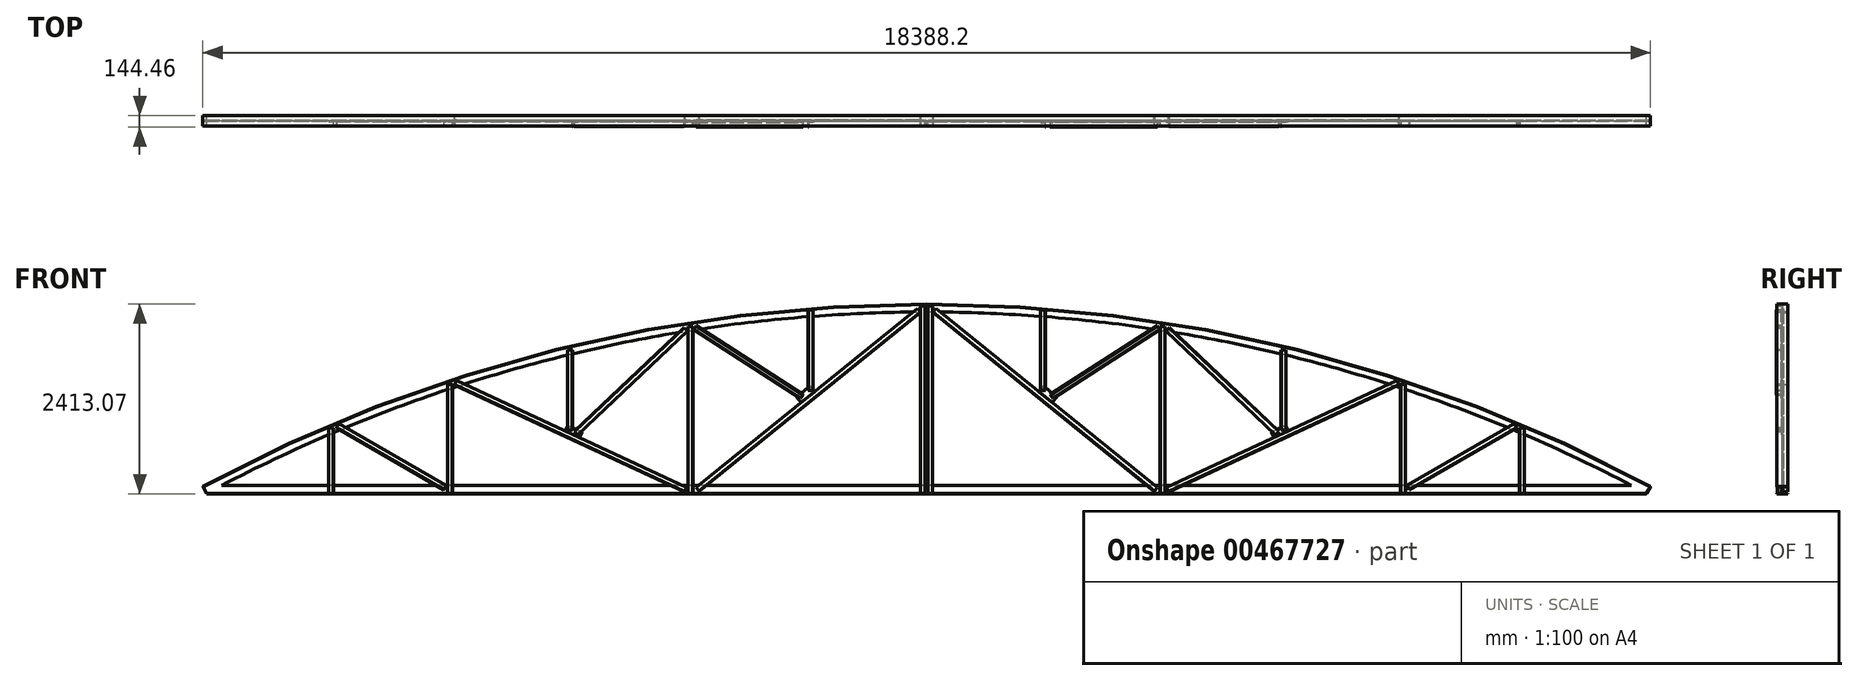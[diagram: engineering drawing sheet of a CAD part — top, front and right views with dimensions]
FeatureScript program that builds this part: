
annotation { "Feature Type Name" : "Feature", "Feature Type Description" : "" }
export const myFeature = defineFeature(function(context is Context, id is Id, definition is map)
    precondition{}
    {
        {
            var Q0;
            Q0=qCreatedBy(makeId("Front.planeOp"),FACE);
            var sketch = newSketch(context, id + "F0", { "sketchPlane" : qUnion([Q0])});
            skLineSegment(sketch, "E0", {"start": v(0, 0) * mm, "end": v(18288, 0) * mm});
            skArc(sketch, "E1", {"start": v(18288, 0) * mm, "mid": v(9144, 2305.05) * mm, "end": v(0, 0) * mm});
            skLineSegment(sketch, "E2", {"start": v(1612.9, 0) * mm, "end": v(1612.9, 774.13) * mm});
            skLineSegment(sketch, "E3", {"start": v(3092.45, 0) * mm, "end": v(3092.45, 1331.2) * mm});
            skLineSegment(sketch, "E4", {"start": v(6115.05, 0) * mm, "end": v(6115.05, 2065.75) * mm});
            skLineSegment(sketch, "E5", {"start": v(9144, 0) * mm, "end": v(9144, 2305.05) * mm});
            skLineSegment(sketch, "E6", {"start": v(7629.52, 1223.6) * mm, "end": v(7629.52, 2245.5) * mm});
            skLineSegment(sketch, "E7", {"start": v(3092.45, 0) * mm, "end": v(1692.88, 807.83) * mm});
            skLineSegment(sketch, "E8", {"start": v(6115.05, 0) * mm, "end": v(3187.59, 1362.37) * mm});
            skLineSegment(sketch, "E9", {"start": v(4651.32, 681.18) * mm, "end": v(4651.32, 1774.56) * mm});
            skLineSegment(sketch, "E10", {"start": v(4651.32, 681.18) * mm, "end": v(6115.05, 2065.75) * mm});
            skLineSegment(sketch, "E11", {"start": v(6190.76, 2077.64) * mm, "end": v(7580.54, 1184.02) * mm});
            skLineSegment(sketch, "E12.MirrorCS", {"start": v(12172.95, 0) * mm, "end": v(9144, 2305.05) * mm});
            skLineSegment(sketch, "E13.MirrorCS", {"start": v(10658.47, 1152.53) * mm, "end": v(10658.47, 2245.5) * mm});
            skLineSegment(sketch, "E14.MirrorCS", {"start": v(12097.24, 2077.64) * mm, "end": v(10658.47, 1152.52) * mm});
            skLineSegment(sketch, "E15.MirrorCS", {"start": v(12172.95, 0) * mm, "end": v(12172.95, 2065.75) * mm});
            skLineSegment(sketch, "E16.MirrorCS", {"start": v(13636.68, 681.18) * mm, "end": v(12172.95, 2065.75) * mm});
            skLineSegment(sketch, "E17.MirrorCS", {"start": v(13636.68, 681.18) * mm, "end": v(13636.68, 1774.56) * mm});
            skLineSegment(sketch, "E18.MirrorCS", {"start": v(12172.95, 0) * mm, "end": v(15100.41, 1362.37) * mm});
            skLineSegment(sketch, "E19.MirrorCS", {"start": v(15195.55, 0) * mm, "end": v(15195.55, 1331.2) * mm});
            skLineSegment(sketch, "E20.MirrorCS", {"start": v(15195.55, 0) * mm, "end": v(16595.12, 807.83) * mm});
            skLineSegment(sketch, "E21.MirrorCS", {"start": v(16675.1, 0) * mm, "end": v(16675.1, 774.13) * mm});
            skLineSegment(sketch, "E22", {"start": v(6115.05, 0) * mm, "end": v(8967.06, 2304.24) * mm});
            skPoint(sketch, "E23.end.orphan", {"position": v(7629.52, 1152.53) * mm});
            skSolve(sketch);
        }
        {
            var Q0;
            Q0=qCreatedBy(makeId("Right.planeOp"),FACE);
            var sketch = newSketch(context, id + "F1", { "sketchPlane" : qUnion([Q0])});
            skLineSegment(sketch, "E24.bottom", {"start": v(-68.26, -3.18) * mm, "end": v(68.26, -3.18) * mm});
            skLineSegment(sketch, "E24.top", {"start": v(-68.26, 3.18) * mm, "end": v(-3.17, 3.18) * mm});
            skLineSegment(sketch, "E24.left", {"start": v(-68.26, -3.18) * mm, "end": v(-68.26, 3.18) * mm});
            skLineSegment(sketch, "E24.right", {"start": v(68.26, -3.18) * mm, "end": v(68.26, 3.18) * mm});
            skPoint(sketch, "E24.middle", {"position": v(0, 0) * mm});
            skLineSegment(sketch, "E25.top", {"start": v(-3.18, 104.78) * mm, "end": v(3.17, 104.78) * mm});
            skLineSegment(sketch, "E25.left", {"start": v(-3.17, 3.18) * mm, "end": v(-3.18, 104.78) * mm});
            skLineSegment(sketch, "E25.right", {"start": v(3.18, 3.18) * mm, "end": v(3.17, 104.78) * mm});
            skLineSegment(sketch, "E26.trimOffspring", {"start": v(3.17, 3.18) * mm, "end": v(68.26, 3.18) * mm});
            skSolve(sketch);
        }
        {
            var Q0;
            Q0=qSketchRegion(id+"F1",true);
            var Q1;
            Q1=sQuery(id+"F0.wireOp",VERTEX,"E1.start");
            extrude(context, id + "F2", {"entities" : qUnion([Q0]), "endBound" : BoundingType.UP_TO_VERTEX, "endBoundEntityVertex" : qUnion([Q1]), "depth" : 25.4 * mm});
        }
        {
            var Q0;
            Q0=sQuery(id+"F0.wireOp",EDGE,"E1");
            var Q1;
            Q1=sQuery(id+"F0.wireOp",VERTEX,"E0.start");
            cPlane(context, id + "F3", {"entities" : qUnion([Q0, Q1]), "cplaneType" : CPlaneType.CURVE_POINT, "offset" : 25.4 * mm, "width" : 152.4 * mm, "height" : 152.4 * mm});
        }
        {
            var Q0;
            Q0=qCreatedBy(id+"F3.planeOp",FACE);
            var sketch = newSketch(context, id + "F4", { "sketchPlane" : qUnion([Q0])});
            skPoint(sketch, "E27.middle", {"position": v(0, 0) * mm});
            skLineSegment(sketch, "E28.left", {"start": v(3.18, 3.25) * mm, "end": v(3.17, 98.5) * mm});
            skLineSegment(sketch, "E28.right", {"start": v(-3.17, 3.25) * mm, "end": v(-3.18, 98.5) * mm});
            skLineSegment(sketch, "E29", {"start": v(-3.17, 3.25) * mm, "end": v(3.18, 3.25) * mm});
            skLineSegment(sketch, "E30", {"start": v(68.26, 104.85) * mm, "end": v(68.26, 98.5) * mm});
            skLineSegment(sketch, "E31", {"start": v(68.26, 98.5) * mm, "end": v(3.17, 98.5) * mm});
            skLineSegment(sketch, "E32", {"start": v(-68.26, 104.85) * mm, "end": v(-68.26, 98.5) * mm});
            skLineSegment(sketch, "E33", {"start": v(-68.26, 98.5) * mm, "end": v(-3.18, 98.5) * mm});
            skPoint(sketch, "E34.0", {"position": v(68.26, -2.8) * mm});
            skPoint(sketch, "E34.1", {"position": v(-68.26, -2.8) * mm});
            skLineSegment(sketch, "E35", {"start": v(-68.26, 104.85) * mm, "end": v(68.26, 104.85) * mm});
            skSolve(sketch);
        }
        {
            var Q0;
            Q0=makeQuery(id+"F4.imprint","IMPRINT",FACE,{"disambiguationData":[TD([[makeQuery(id+"F4.imprint","IMPRINT",EDGE,{"derivedFrom":sQuery(id+"F4.wireOp",EDGE,"E28.left")}),1.0]])]});
            var Q1;
            Q1=sQuery(id+"F0.wireOp",EDGE,"E1");
            sweep(context, id + "F5", {"profiles" : qUnion([Q0]), "path" : qUnion([Q1])});
        }
        {
            var Q0;
            Q0=sQuery(id+"F0.wireOp",EDGE,"E2");
            var Q1;
            Q1=sQuery(id+"F0.wireOp",VERTEX,"E2.start");
            cPlane(context, id + "F6", {"entities" : qUnion([Q0, Q1]), "cplaneType" : CPlaneType.CURVE_POINT, "offset" : 25.4 * mm, "width" : 152.4 * mm, "height" : 152.4 * mm});
        }
        {
            var Q0;
            Q0=qCreatedBy(id+"F6.planeOp",FACE);
            var sketch = newSketch(context, id + "F7", { "sketchPlane" : qUnion([Q0])});
            skLineSegment(sketch, "E36", {"start": v(1612.9, -66.68) * mm, "end": v(1606.55, -66.68) * mm});
            skLineSegment(sketch, "E37", {"start": v(1606.55, -66.68) * mm, "end": v(1606.55, -9.53) * mm});
            skPoint(sketch, "E38.bottom.start.orphan", {"position": v(1606.55, 0) * mm});
            skLineSegment(sketch, "E39", {"start": v(1612.9, -3.17) * mm, "end": v(1612.9, -66.68) * mm});
            skPoint(sketch, "E40.0", {"position": v(1612.9, 0) * mm});
            skLineSegment(sketch, "E41", {"start": v(1606.55, -9.53) * mm, "end": v(1549.4, -9.53) * mm});
            skLineSegment(sketch, "E42", {"start": v(1549.4, 0) * mm, "end": v(1612.9, 0) * mm});
            skLineSegment(sketch, "E43", {"start": v(1549.4, -3.18) * mm, "end": v(1612.9, -3.17) * mm});
            skPoint(sketch, "E44.start.orphan", {"position": v(1549.4, -6.35) * mm});
            skLineSegment(sketch, "E45", {"start": v(1549.4, -9.53) * mm, "end": v(1549.4, -3.18) * mm});
            skSolve(sketch);
        }
        {
            var Q0;
            Q0=qSketchRegion(id+"F7",true);
            extrude(context, id + "F8", {"entities" : qUnion([Q0]), "operationType" : NewBodyOperationType.ADD, "depth" : 838.2 * mm});
        }
        {
            var Q0;
            Q0=sQuery(id+"F0.wireOp",EDGE,"E7");
            var Q1;
            Q1=sQuery(id+"F0.wireOp",VERTEX,"E3.start");
            cPlane(context, id + "F9", {"entities" : qUnion([Q0, Q1]), "cplaneType" : CPlaneType.CURVE_POINT, "offset" : 25.4 * mm, "width" : 152.4 * mm, "height" : 152.4 * mm});
        }
        {
            var Q0;
            Q0=qCreatedBy(id+"F9.planeOp",FACE);
            var sketch = newSketch(context, id + "F10", { "sketchPlane" : qUnion([Q0])});
            skPoint(sketch, "E46.0", {"position": v(2.83, 1546.43) * mm});
            skLineSegment(sketch, "E47", {"start": v(3.18, 1545.92) * mm, "end": v(66.67, 1545.92) * mm});
            skLineSegment(sketch, "E48", {"start": v(66.67, 1545.92) * mm, "end": v(66.67, 1552.27) * mm});
            skLineSegment(sketch, "E49", {"start": v(66.67, 1552.27) * mm, "end": v(9.52, 1552.27) * mm});
            skLineSegment(sketch, "E50", {"start": v(9.52, 1552.27) * mm, "end": v(9.52, 1609.42) * mm});
            skLineSegment(sketch, "E51", {"start": v(9.52, 1609.42) * mm, "end": v(3.17, 1609.42) * mm});
            skLineSegment(sketch, "E52", {"start": v(3.17, 1609.42) * mm, "end": v(3.17, 1545.92) * mm});
            skSolve(sketch);
        }
        {
            var Q0;
            Q0=qSketchRegion(id+"F10",true);
            extrude(context, id + "F11", {"entities" : qUnion([Q0]), "depth" : 1574.8 * mm});
        }
        {
            var Q0;
            Q0=sQuery(id+"F0.wireOp",EDGE,"E3");
            var Q1;
            Q1=sQuery(id+"F0.wireOp",VERTEX,"E7.start");
            cPlane(context, id + "F12", {"entities" : qUnion([Q0, Q1]), "cplaneType" : CPlaneType.CURVE_POINT, "offset" : 25.4 * mm, "width" : 152.4 * mm, "height" : 152.4 * mm});
        }
        {
            var Q0;
            Q0=qCreatedBy(id+"F12.planeOp",FACE);
            var sketch = newSketch(context, id + "F13", { "sketchPlane" : qUnion([Q0])});
            skLineSegment(sketch, "E53", {"start": v(3124.65, -66.68) * mm, "end": v(3124.65, -9.53) * mm});
            skLineSegment(sketch, "E54", {"start": v(3124.65, -66.67) * mm, "end": v(3118.3, -66.67) * mm});
            skLineSegment(sketch, "E55", {"start": v(3118.3, -9.53) * mm, "end": v(3118.3, -66.67) * mm});
            skLineSegment(sketch, "E56", {"start": v(3118.3, -3.17) * mm, "end": v(3061.15, -3.18) * mm});
            skLineSegment(sketch, "E57", {"start": v(3061.15, -3.18) * mm, "end": v(3061.15, -9.53) * mm});
            skLineSegment(sketch, "E58", {"start": v(3061.15, -9.53) * mm, "end": v(3118.3, -9.53) * mm});
            skLineSegment(sketch, "E59", {"start": v(3124.65, -9.53) * mm, "end": v(3124.65, -3.17) * mm});
            skLineSegment(sketch, "E60", {"start": v(3124.65, -3.17) * mm, "end": v(3118.3, -3.17) * mm});
            skSolve(sketch);
        }
        {
            var Q0;
            Q0=qSketchRegion(id+"F13",true);
            extrude(context, id + "F14", {"entities" : qUnion([Q0]), "depth" : 1386.84 * mm});
        }
        {
            var Q0;
            Q0=makeQuery(id+"F11.opExtrude","SWEPT_BODY",BODY,{"disambiguationData":[OSD([sQuery(id+"F10.wireOp",EDGE,"E47"),sQuery(id+"F10.wireOp",EDGE,"E48"),sQuery(id+"F10.wireOp",EDGE,"E49"),sQuery(id+"F10.wireOp",EDGE,"E50"),sQuery(id+"F10.wireOp",EDGE,"E51"),sQuery(id+"F10.wireOp",EDGE,"E52")])]});
            var Q1;
            Q1=sQuery(id+"F0.wireOp",EDGE,"E7");
            var Q2;
            Q2=sQuery(id+"F0.wireOp",EDGE,"E7");
            transform(context, id + "F15", {"entities" : qUnion([Q0]), "transformType" : TransformType.TRANSLATION_DISTANCE, "transformDirection" : qUnion([Q2]), "distance" : 95.25 * mm, "makeCopy" : false});
        }
        {
            var Q0;
            Q0=sQuery(id+"F0.wireOp",EDGE,"E8");
            var Q1;
            Q1=sQuery(id+"F0.wireOp",VERTEX,"E8.start");
            cPlane(context, id + "F16", {"entities" : qUnion([Q0, Q1]), "cplaneType" : CPlaneType.CURVE_POINT, "offset" : 25.4 * mm, "width" : 152.4 * mm, "height" : 152.4 * mm});
        }
        {
            var Q0;
            Q0=qCreatedBy(id+"F16.planeOp",FACE);
            cPlane(context, id + "F17", {"entities" : qUnion([Q0]), "cplaneType" : CPlaneType.OFFSET, "offset" : 50.8 * mm, "width" : 152.4 * mm, "height" : 152.4 * mm});
        }
        {
            var Q0;
            Q0=qCreatedBy(id+"F17.planeOp",FACE);
            var sketch = newSketch(context, id + "F18", { "sketchPlane" : qUnion([Q0])});
            skPoint(sketch, "E61.0", {"position": v(0, 2580.09) * mm});
            skLineSegment(sketch, "E62.MirrorCS", {"start": v(-3.18, 2580.09) * mm, "end": v(-3.18, 2643.59) * mm});
            skLineSegment(sketch, "E63.MirrorCS", {"start": v(-3.18, 2643.59) * mm, "end": v(-9.53, 2643.59) * mm});
            skLineSegment(sketch, "E64.MirrorCS", {"start": v(-9.53, 2643.59) * mm, "end": v(-9.53, 2586.44) * mm});
            skLineSegment(sketch, "E65.MirrorCS", {"start": v(-9.53, 2586.44) * mm, "end": v(-66.67, 2586.44) * mm});
            skLineSegment(sketch, "E66.MirrorCS", {"start": v(-66.67, 2586.44) * mm, "end": v(-66.67, 2580.09) * mm});
            skLineSegment(sketch, "E67.MirrorCS", {"start": v(-66.67, 2580.09) * mm, "end": v(-3.18, 2580.09) * mm});
            skLineSegment(sketch, "E68.MirrorCS", {"start": v(3.18, 2643.59) * mm, "end": v(9.53, 2643.59) * mm});
            skLineSegment(sketch, "E69.MirrorCS", {"start": v(66.67, 2586.44) * mm, "end": v(66.67, 2580.09) * mm});
            skLineSegment(sketch, "E70.MirrorCS", {"start": v(66.67, 2580.09) * mm, "end": v(3.18, 2580.09) * mm});
            skLineSegment(sketch, "E71.MirrorCS", {"start": v(3.18, 2580.09) * mm, "end": v(3.18, 2643.59) * mm});
            skLineSegment(sketch, "E72.MirrorCS", {"start": v(9.53, 2586.44) * mm, "end": v(66.67, 2586.44) * mm});
            skLineSegment(sketch, "E73.MirrorCS", {"start": v(9.53, 2643.59) * mm, "end": v(9.53, 2586.44) * mm});
            skSolve(sketch);
        }
        {
            var Q0;
            Q0=qSketchRegion(id+"F18",true);
            extrude(context, id + "F19", {"entities" : qUnion([Q0]), "depth" : 3225.8 * mm});
        }
        {
            var Q0;
            Q0=sQuery(id+"F0.wireOp",EDGE,"E8");
            cPoint(context, id + "F20", {"entities" : qUnion([Q0]), "parameter" : 0.5});
        }
        {
            var Q0;
            Q0=sQuery(id+"F0.wireOp",EDGE,"E9");
            var Q1;
            Q1=qCreatedBy(id+"F20",VERTEX);
            cPlane(context, id + "F21", {"entities" : qUnion([Q0, Q1]), "cplaneType" : CPlaneType.CURVE_POINT, "offset" : 25.4 * mm, "width" : 152.4 * mm, "height" : 152.4 * mm});
        }
        {
            var Q0;
            Q0=qCreatedBy(id+"F21.planeOp",FACE);
            cPlane(context, id + "F22", {"entities" : qUnion([Q0]), "cplaneType" : CPlaneType.OFFSET, "offset" : 127 * mm, "width" : 152.4 * mm, "height" : 152.4 * mm});
        }
        {
            var Q0;
            Q0=qCreatedBy(id+"F22.planeOp",FACE);
            var sketch = newSketch(context, id + "F23", { "sketchPlane" : qUnion([Q0])});
            skLineSegment(sketch, "E74", {"start": v(4644.56, -9.53) * mm, "end": v(4644.56, -73.03) * mm});
            skLineSegment(sketch, "E75", {"start": v(4644.56, -73.03) * mm, "end": v(4638.21, -73.03) * mm});
            skLineSegment(sketch, "E76", {"start": v(4638.21, -73.03) * mm, "end": v(4638.21, -15.88) * mm});
            skLineSegment(sketch, "E77", {"start": v(4638.21, -15.88) * mm, "end": v(4581.06, -15.88) * mm});
            skLineSegment(sketch, "E78", {"start": v(4581.06, -15.88) * mm, "end": v(4581.06, -9.53) * mm});
            skLineSegment(sketch, "E79", {"start": v(4581.06, -9.53) * mm, "end": v(4644.56, -9.53) * mm});
            skLineSegment(sketch, "E80.0", {"start": v(3144.76, -9.53) * mm, "end": v(6117.73, -9.53) * mm});
            skSolve(sketch);
        }
        {
            var Q0;
            Q0=qSketchRegion(id+"F23",true);
            extrude(context, id + "F24", {"entities" : qUnion([Q0]), "operationType" : NewBodyOperationType.ADD, "depth" : 1016 * mm});
        }
        {
            var Q0;
            Q0=sQuery(id+"F0.wireOp",EDGE,"E10");
            var Q1;
            Q1=sQuery(id+"F0.wireOp",VERTEX,"E10.start");
            cPlane(context, id + "F25", {"entities" : qUnion([Q0, Q1]), "cplaneType" : CPlaneType.CURVE_POINT, "offset" : 25.4 * mm, "width" : 152.4 * mm, "height" : 152.4 * mm});
        }
        {
            var Q0;
            Q0=qCreatedBy(id+"F25.planeOp",FACE);
            cPlane(context, id + "F26", {"entities" : qUnion([Q0]), "cplaneType" : CPlaneType.OFFSET, "offset" : 88.9 * mm, "width" : 152.4 * mm, "height" : 152.4 * mm});
        }
        {
            var Q0;
            Q0=qCreatedBy(id+"F26.planeOp",FACE);
            var sketch = newSketch(context, id + "F27", { "sketchPlane" : qUnion([Q0])});
            skLineSegment(sketch, "E81.0", {"start": v(0.48, -1133.42) * mm, "end": v(0.48, -4181.53) * mm});
            skLineSegment(sketch, "E82", {"start": v(-9.05, -2695.12) * mm, "end": v(-9.05, -2631.62) * mm});
            skLineSegment(sketch, "E83", {"start": v(-9.05, -2631.62) * mm, "end": v(-72.55, -2631.62) * mm});
            skLineSegment(sketch, "E84", {"start": v(-72.55, -2631.62) * mm, "end": v(-72.55, -2637.97) * mm});
            skLineSegment(sketch, "E85", {"start": v(-72.55, -2637.97) * mm, "end": v(-15.4, -2637.97) * mm});
            skLineSegment(sketch, "E86", {"start": v(-15.4, -2637.97) * mm, "end": v(-15.4, -2695.12) * mm});
            skLineSegment(sketch, "E87", {"start": v(-15.4, -2695.12) * mm, "end": v(-9.05, -2695.12) * mm});
            skPoint(sketch, "E88.end.orphan", {"position": v(13.18, -2683.97) * mm});
            skSolve(sketch);
        }
        {
            var Q0;
            Q0=qSketchRegion(id+"F27",true);
            extrude(context, id + "F28", {"entities" : qUnion([Q0]), "depth" : 1917.7 * mm});
        }
        {
            var Q0;
            Q0=makeQuery(id+"F19.opExtrude","SWEPT_FACE",FACE,{"disambiguationData":[OSD([sQuery(id+"F18.wireOp",EDGE,"E68.MirrorCS")])]});
            var sketch = newSketch(context, id + "F29", { "sketchPlane" : qUnion([Q0])});
            skLineSegment(sketch, "E89.bottom", {"start": v(3789.84, -9.53) * mm, "end": v(3993.04, -9.53) * mm});
            skLineSegment(sketch, "E89.top", {"start": v(3789.84, -3.17) * mm, "end": v(3993.04, -3.17) * mm});
            skLineSegment(sketch, "E89.left", {"start": v(3789.84, -9.53) * mm, "end": v(3789.84, -3.17) * mm});
            skLineSegment(sketch, "E89.right", {"start": v(3993.04, -9.53) * mm, "end": v(3993.04, -3.17) * mm});
            skSolve(sketch);
        }
        {
            var Q0;
            Q0=qSketchRegion(id+"F29",true);
            extrude(context, id + "F30", {"entities" : qUnion([Q0]), "depth" : 76.96 * mm});
        }
        {
            var Q0;
            Q0=makeQuery(id+"F2.opExtrude","SWEPT_FACE",FACE,{"disambiguationData":[OSD([sQuery(id+"F1.wireOp",EDGE,"E24.top")])]});
            cPlane(context, id + "F31", {"entities" : qUnion([Q0]), "cplaneType" : CPlaneType.OFFSET, "offset" : 0 * mm, "width" : 152.4 * mm, "height" : 152.4 * mm});
        }
        {
            var Q0;
            Q0=qCreatedBy(id+"F31.planeOp",FACE);
            var sketch = newSketch(context, id + "F32", { "sketchPlane" : qUnion([Q0])});
            skPoint(sketch, "E90.0", {"position": v(6115.05, 0) * mm});
            skLineSegment(sketch, "E91", {"start": v(6115.05, -3.18) * mm, "end": v(6178.55, -3.18) * mm});
            skLineSegment(sketch, "E92", {"start": v(6178.55, -3.18) * mm, "end": v(6178.55, -9.53) * mm});
            skLineSegment(sketch, "E93", {"start": v(6115.05, -9.53) * mm, "end": v(6115.05, -3.17) * mm});
            skLineSegment(sketch, "E94", {"start": v(6178.55, -9.53) * mm, "end": v(6178.55, -66.67) * mm});
            skLineSegment(sketch, "E95", {"start": v(6178.55, -66.67) * mm, "end": v(6172.2, -66.67) * mm});
            skLineSegment(sketch, "E96", {"start": v(6172.2, -66.67) * mm, "end": v(6172.2, -9.53) * mm});
            skPoint(sketch, "E97.start.orphan", {"position": v(6122.79, -66.68) * mm});
            skPoint(sketch, "E98.orphan", {"position": v(6115.05, -66.67) * mm});
            skLineSegment(sketch, "E99", {"start": v(6115.05, -9.53) * mm, "end": v(6172.2, -9.53) * mm});
            skSolve(sketch);
        }
        {
            var Q0;
            Q0=qSketchRegion(id+"F32",true);
            extrude(context, id + "F33", {"entities" : qUnion([Q0]), "depth" : 2120.9 * mm});
        }
        {
            var Q0;
            Q0=makeQuery(id+"F2.opExtrude","SWEPT_FACE",FACE,{"disambiguationData":[OSD([sQuery(id+"F1.wireOp",EDGE,"E24.top")])]});
            var sketch = newSketch(context, id + "F34", { "sketchPlane" : qUnion([Q0])});
            skPoint(sketch, "E100.0", {"position": v(9144, 0) * mm});
            skLineSegment(sketch, "E101.0", {"start": v(0, 0) * mm, "end": v(18288, 0) * mm});
            skLineSegment(sketch, "E102", {"start": v(9131.7, -3.17) * mm, "end": v(9131.7, -66.67) * mm});
            skLineSegment(sketch, "E103", {"start": v(9131.7, -66.67) * mm, "end": v(9125.35, -66.67) * mm});
            skLineSegment(sketch, "E104", {"start": v(9125.35, -66.67) * mm, "end": v(9125.35, -9.52) * mm});
            skLineSegment(sketch, "E105", {"start": v(9125.35, -9.52) * mm, "end": v(9068.2, -9.53) * mm});
            skLineSegment(sketch, "E106", {"start": v(9068.2, -9.53) * mm, "end": v(9068.2, -3.18) * mm});
            skLineSegment(sketch, "E107", {"start": v(9068.2, -3.17) * mm, "end": v(9131.7, -3.17) * mm});
            skSolve(sketch);
        }
        {
            var Q0;
            Q0=makeQuery(id+"F34.imprint","IMPRINT",FACE,{"disambiguationData":[TD([[makeQuery(id+"F34.imprint","IMPRINT",EDGE,{"derivedFrom":sQuery(id+"F34.wireOp",EDGE,"E102")}),-1.0]])]});
            extrude(context, id + "F35", {"entities" : qUnion([Q0]), "operationType" : NewBodyOperationType.ADD, "depth" : 2379.98 * mm});
        }
        {
            var Q0;
            Q0=sQuery(id+"F0.wireOp",EDGE,"E22");
            var Q1;
            Q1=sQuery(id+"F0.wireOp",VERTEX,"E4.start");
            cPlane(context, id + "F36", {"entities" : qUnion([Q0, Q1]), "cplaneType" : CPlaneType.CURVE_POINT, "offset" : 25.4 * mm, "width" : 152.4 * mm, "height" : 152.4 * mm});
        }
        {
            var Q0;
            Q0=qCreatedBy(id+"F36.planeOp",FACE);
            cPlane(context, id + "F37", {"entities" : qUnion([Q0]), "cplaneType" : CPlaneType.OFFSET, "offset" : 129.54 * mm, "width" : 152.4 * mm, "height" : 152.4 * mm});
        }
        {
            var Q0;
            Q0=qCreatedBy(id+"F37.planeOp",FACE);
            var sketch = newSketch(context, id + "F38", { "sketchPlane" : qUnion([Q0])});
            skPoint(sketch, "E108.0", {"position": v(0, -3843) * mm});
            skLineSegment(sketch, "E109", {"start": v(0, -3843) * mm, "end": v(-4.09, -3843) * mm});
            skLineSegment(sketch, "E110", {"start": v(-4.09, -3843) * mm, "end": v(-4.09, -3906.5) * mm});
            skLineSegment(sketch, "E111", {"start": v(-4.09, -3906.5) * mm, "end": v(-67.59, -3906.5) * mm});
            skLineSegment(sketch, "E112", {"start": v(-67.59, -3906.5) * mm, "end": v(-67.59, -3900.16) * mm});
            skLineSegment(sketch, "E113", {"start": v(-67.59, -3900.16) * mm, "end": v(-10.44, -3900.16) * mm});
            skLineSegment(sketch, "E114", {"start": v(-10.44, -3900.16) * mm, "end": v(-10.44, -3843) * mm});
            skLineSegment(sketch, "E115", {"start": v(-10.44, -3843) * mm, "end": v(-4.09, -3843) * mm});
            skLineSegment(sketch, "E116.MirrorCS", {"start": v(4.09, -3843) * mm, "end": v(4.09, -3906.5) * mm});
            skLineSegment(sketch, "E117.MirrorCS", {"start": v(10.44, -3900.16) * mm, "end": v(10.44, -3843) * mm});
            skLineSegment(sketch, "E118.MirrorCS", {"start": v(67.59, -3900.16) * mm, "end": v(10.44, -3900.16) * mm});
            skLineSegment(sketch, "E119.MirrorCS", {"start": v(10.44, -3843) * mm, "end": v(4.09, -3843) * mm});
            skLineSegment(sketch, "E120.MirrorCS", {"start": v(4.09, -3906.5) * mm, "end": v(67.59, -3906.5) * mm});
            skLineSegment(sketch, "E121.MirrorCS", {"start": v(67.59, -3906.5) * mm, "end": v(67.59, -3900.16) * mm});
            skSolve(sketch);
        }
        {
            var Q0;
            Q0=qSketchRegion(id+"F38",true);
            extrude(context, id + "F39", {"entities" : qUnion([Q0]), "depth" : 3614.42 * mm});
        }
        {
            var Q0;
            Q0=sQuery(id+"F0.wireOp",EDGE,"E6");
            var Q1;
            Q1=sQuery(id+"F0.wireOp",VERTEX,"E23.end.orphan");
            cPlane(context, id + "F40", {"entities" : qUnion([Q0, Q1]), "cplaneType" : CPlaneType.CURVE_POINT, "offset" : 25.4 * mm, "width" : 152.4 * mm, "height" : 152.4 * mm});
        }
        {
            var Q0;
            Q0=qCreatedBy(id+"F40.planeOp",FACE);
            cPlane(context, id + "F41", {"entities" : qUnion([Q0]), "cplaneType" : CPlaneType.OFFSET, "offset" : 157.48 * mm, "width" : 152.4 * mm, "height" : 152.4 * mm});
        }
        {
            var Q0;
            Q0=qCreatedBy(id+"F41.planeOp",FACE);
            var sketch = newSketch(context, id + "F42", { "sketchPlane" : qUnion([Q0])});
            skLineSegment(sketch, "E122", {"start": v(7638.44, -76.2) * mm, "end": v(7638.44, -12.7) * mm});
            skLineSegment(sketch, "E123", {"start": v(7638.44, -76.2) * mm, "end": v(7644.79, -76.2) * mm});
            skLineSegment(sketch, "E124", {"start": v(7644.79, -19.05) * mm, "end": v(7644.79, -76.2) * mm});
            skLineSegment(sketch, "E125", {"start": v(7701.94, 0) * mm, "end": v(7638.44, 0) * mm});
            skLineSegment(sketch, "E126", {"start": v(7638.44, 0) * mm, "end": v(7701.94, 0) * mm});
            skPoint(sketch, "E127.0", {"position": v(7629.52, 0) * mm});
            skLineSegment(sketch, "E128", {"start": v(7701.94, -19.05) * mm, "end": v(7644.79, -19.05) * mm});
            skLineSegment(sketch, "E129", {"start": v(7701.94, -12.7) * mm, "end": v(7701.94, -19.05) * mm});
            skLineSegment(sketch, "E130", {"start": v(7638.44, -12.7) * mm, "end": v(7701.94, -12.7) * mm});
            skSolve(sketch);
        }
        {
            var Q0;
            Q0=qSketchRegion(id+"F42",true);
            extrude(context, id + "F43", {"entities" : qUnion([Q0]), "operationType" : NewBodyOperationType.ADD, "depth" : 1021.08 * mm});
        }
        {
            var Q0;
            Q0=sQuery(id+"F0.wireOp",EDGE,"E11");
            var Q1;
            Q1=sQuery(id+"F0.wireOp",VERTEX,"E23.end.orphan");
            cPlane(context, id + "F44", {"entities" : qUnion([Q0, Q1]), "cplaneType" : CPlaneType.CURVE_POINT, "offset" : 25.4 * mm, "width" : 152.4 * mm, "height" : 152.4 * mm});
        }
        {
            var Q0;
            Q0=qCreatedBy(id+"F44.planeOp",FACE);
            cPlane(context, id + "F45", {"entities" : qUnion([Q0]), "cplaneType" : CPlaneType.OFFSET, "offset" : 104.14 * mm, "oppositeDirection" : true, "width" : 152.4 * mm, "height" : 152.4 * mm});
        }
        {
            var Q0;
            Q0=qCreatedBy(id+"F45.planeOp",FACE);
            var sketch = newSketch(context, id + "F46", { "sketchPlane" : qUnion([Q0])});
            skLineSegment(sketch, "E131.0.1", {"start": v(0, 5095.74) * mm, "end": v(0, 5155.52) * mm});
            skLineSegment(sketch, "E131.0.2", {"start": v(0, 5155.52) * mm, "end": v(0, 6015.07) * mm});
            skLineSegment(sketch, "E131.0.3", {"start": v(0, 6015.07) * mm, "end": v(0, 5095.74) * mm});
            skLineSegment(sketch, "E132", {"start": v(-12.7, 5159.52) * mm, "end": v(-76.2, 5159.52) * mm});
            skLineSegment(sketch, "E133", {"start": v(-76.2, 5159.52) * mm, "end": v(-76.2, 5153.17) * mm});
            skLineSegment(sketch, "E134", {"start": v(-76.2, 5153.17) * mm, "end": v(-19.05, 5153.17) * mm});
            skLineSegment(sketch, "E135", {"start": v(-19.05, 5153.17) * mm, "end": v(-19.05, 5096.15) * mm});
            skLineSegment(sketch, "E136", {"start": v(-19.05, 5096.15) * mm, "end": v(-12.7, 5096.02) * mm});
            skLineSegment(sketch, "E137", {"start": v(0, 5159.52) * mm, "end": v(0, 5095.74) * mm});
            skLineSegment(sketch, "E138", {"start": v(-12.7, 5096.02) * mm, "end": v(-12.7, 5159.52) * mm});
            skSolve(sketch);
        }
        {
            var Q0;
            Q0=qSketchRegion(id+"F46",true);
            extrude(context, id + "F47", {"entities" : qUnion([Q0]), "operationType" : NewBodyOperationType.ADD, "oppositeDirection" : true, "depth" : 1617.98 * mm});
        }
        {
            var Q0;
            Q0=makeQuery(id+"F39.opExtrude","SWEPT_FACE",FACE,{"disambiguationData":[OSD([sQuery(id+"F38.wireOp",EDGE,"E115")])]});
            var sketch = newSketch(context, id + "F48", { "sketchPlane" : qUnion([Q0])});
            skLineSegment(sketch, "E139.bottom", {"start": v(6601.21, -10.44) * mm, "end": v(6817.11, -10.44) * mm});
            skLineSegment(sketch, "E139.top", {"start": v(6601.21, -4.09) * mm, "end": v(6817.11, -4.09) * mm});
            skLineSegment(sketch, "E139.left", {"start": v(6601.21, -10.44) * mm, "end": v(6601.21, -4.09) * mm});
            skLineSegment(sketch, "E139.right", {"start": v(6817.11, -10.44) * mm, "end": v(6817.11, -4.09) * mm});
            skSolve(sketch);
        }
        {
            var Q0;
            Q0=qSketchRegion(id+"F48",true);
            extrude(context, id + "F49", {"entities" : qUnion([Q0]), "depth" : 91.44 * mm});
        }
        {
            var Q0;
            Q0=makeQuery(id+"F35.opExtrude","SWEPT_FACE",FACE,{"disambiguationData":[OSD([sQuery(id+"F34.wireOp",EDGE,"E102")])]});
            cPlane(context, id + "F50", {"entities" : qUnion([Q0]), "cplaneType" : CPlaneType.OFFSET, "offset" : 12.7 * mm, "width" : 152.4 * mm, "height" : 152.4 * mm});
        }
        {
            var Q0;
            Q0=makeQuery(id+"F39.opExtrude","SWEPT_BODY",BODY,{"disambiguationData":[OSD([sQuery(id+"F38.wireOp",EDGE,"E110"),sQuery(id+"F38.wireOp",EDGE,"E111"),sQuery(id+"F38.wireOp",EDGE,"E112"),sQuery(id+"F38.wireOp",EDGE,"E113"),sQuery(id+"F38.wireOp",EDGE,"E114"),sQuery(id+"F38.wireOp",EDGE,"E115")])]});
            var Q1;
            Q1=makeQuery(id+"F43.opExtrude","SWEPT_BODY",BODY,{"disambiguationData":[OSD([sQuery(id+"F42.wireOp",EDGE,"E122"),sQuery(id+"F42.wireOp",EDGE,"E123"),sQuery(id+"F42.wireOp",EDGE,"E124"),sQuery(id+"F42.wireOp",EDGE,"uOuj5NGx-17GM-Mw7A-FTPI-DWF7fpRwAIm5"),sQuery(id+"F42.wireOp",EDGE,"dZkJSmds-j7UH-SSCP-u4Ih-RMBNkNQA11X7"),sQuery(id+"F42.wireOp",EDGE,"E126")])]});
            var Q2;
            Q2=makeQuery(id+"F49.opExtrude","SWEPT_BODY",BODY,{"disambiguationData":[OSD([sQuery(id+"F48.wireOp",EDGE,"E139.bottom"),sQuery(id+"F48.wireOp",EDGE,"E139.top"),sQuery(id+"F48.wireOp",EDGE,"E139.left"),sQuery(id+"F48.wireOp",EDGE,"E139.right")])]});
            var Q3;
            Q3=makeQuery(id+"F5.opSweep","SWEPT_BODY",BODY,{"disambiguationData":[OSD([sQuery(id+"F0.wireOp",EDGE,"E1"),sQuery(id+"F4.wireOp",EDGE,"E28.left"),sQuery(id+"F4.wireOp",EDGE,"E28.right"),sQuery(id+"F4.wireOp",EDGE,"E29"),sQuery(id+"F4.wireOp",EDGE,"E30"),sQuery(id+"F4.wireOp",EDGE,"E31"),sQuery(id+"F4.wireOp",EDGE,"E32"),sQuery(id+"F4.wireOp",EDGE,"E33"),sQuery(id+"F4.wireOp",EDGE,"E35")])]});
            var Q4;
            Q4=makeQuery(id+"F33.opExtrude","SWEPT_BODY",BODY,{"disambiguationData":[OSD([sQuery(id+"F32.wireOp",EDGE,"E91"),sQuery(id+"F32.wireOp",EDGE,"E92"),sQuery(id+"F32.wireOp",EDGE,"E93"),sQuery(id+"F32.wireOp",EDGE,"E94"),sQuery(id+"F32.wireOp",EDGE,"E95"),sQuery(id+"F32.wireOp",EDGE,"E96"),sQuery(id+"F32.wireOp",EDGE,"E99")])]});
            var Q5;
            Q5=makeQuery(id+"F28.opExtrude","SWEPT_BODY",BODY,{"disambiguationData":[OSD([sQuery(id+"F27.wireOp",EDGE,"E82"),sQuery(id+"F27.wireOp",EDGE,"E83"),sQuery(id+"F27.wireOp",EDGE,"E84"),sQuery(id+"F27.wireOp",EDGE,"E85"),sQuery(id+"F27.wireOp",EDGE,"E86"),sQuery(id+"F27.wireOp",EDGE,"E87")])]});
            var Q6;
            Q6=makeQuery(id+"F19.opExtrude","SWEPT_BODY",BODY,{"disambiguationData":[OSD([sQuery(id+"F18.wireOp",EDGE,"fR6K2I5n-3yyS-XcYj-GziI-SimCiqrJYMnS"),sQuery(id+"F18.wireOp",EDGE,"DomAPrI3-vOdW-qizV-5RqZ-W5uNoyG2PKUz"),sQuery(id+"F18.wireOp",EDGE,"gMHwrGF1-JGd2-y6CO-m9wL-YWMoOy4B9Btv"),sQuery(id+"F18.wireOp",EDGE,"1H9iAEpe-uR8N-W58M-Nnsx-awdP13kMLbvY"),sQuery(id+"F18.wireOp",EDGE,"WdFXNTIy-uckv-oNBa-KU6S-SmvUdIfRYj6D"),sQuery(id+"F18.wireOp",EDGE,"QOBKChic-byfR-FNSD-CDCA-rWGsIW7gaVbq")])]});
            var Q7;
            Q7=makeQuery(id+"F24.opExtrude","SWEPT_BODY",BODY,{"disambiguationData":[OSD([sQuery(id+"F23.wireOp",EDGE,"E74"),sQuery(id+"F23.wireOp",EDGE,"E75"),sQuery(id+"F23.wireOp",EDGE,"E76"),sQuery(id+"F23.wireOp",EDGE,"E77"),sQuery(id+"F23.wireOp",EDGE,"E78"),sQuery(id+"F23.wireOp",EDGE,"E80.0")])]});
            var Q8;
            Q8=makeQuery(id+"F14.opExtrude","SWEPT_BODY",BODY,{"disambiguationData":[OSD([sQuery(id+"F13.wireOp",EDGE,"E53"),sQuery(id+"F13.wireOp",EDGE,"E54"),sQuery(id+"F13.wireOp",EDGE,"E55"),sQuery(id+"F13.wireOp",EDGE,"E56"),sQuery(id+"F13.wireOp",EDGE,"E57"),sQuery(id+"F13.wireOp",EDGE,"E58"),sQuery(id+"F13.wireOp",EDGE,"E59"),sQuery(id+"F13.wireOp",EDGE,"E60")])]});
            var Q9;
            Q9=makeQuery(id+"F11.opExtrude","SWEPT_BODY",BODY,{"disambiguationData":[OSD([sQuery(id+"F10.wireOp",EDGE,"E47"),sQuery(id+"F10.wireOp",EDGE,"E48"),sQuery(id+"F10.wireOp",EDGE,"E49"),sQuery(id+"F10.wireOp",EDGE,"E50"),sQuery(id+"F10.wireOp",EDGE,"E51"),sQuery(id+"F10.wireOp",EDGE,"E52")])]});
            var Q10;
            Q10=makeQuery(id+"F2.opExtrude","SWEPT_BODY",BODY,{"disambiguationData":[OSD([sQuery(id+"F1.wireOp",EDGE,"E24.bottom"),sQuery(id+"F1.wireOp",EDGE,"E24.top"),sQuery(id+"F1.wireOp",EDGE,"E24.left"),sQuery(id+"F1.wireOp",EDGE,"E24.right"),sQuery(id+"F1.wireOp",EDGE,"E25.top"),sQuery(id+"F1.wireOp",EDGE,"E25.left"),sQuery(id+"F1.wireOp",EDGE,"E25.right"),sQuery(id+"F1.wireOp",EDGE,"E26.trimOffspring")])]});
            var Q11;
            Q11=makeQuery(id+"F39.opExtrude","SWEPT_BODY",BODY,{"disambiguationData":[OSD([sQuery(id+"F38.wireOp",EDGE,"E116.MirrorCS"),sQuery(id+"F38.wireOp",EDGE,"E117.MirrorCS"),sQuery(id+"F38.wireOp",EDGE,"E118.MirrorCS"),sQuery(id+"F38.wireOp",EDGE,"E119.MirrorCS"),sQuery(id+"F38.wireOp",EDGE,"E120.MirrorCS"),sQuery(id+"F38.wireOp",EDGE,"E121.MirrorCS")])]});
            var Q12;
            Q12=makeQuery(id+"F19.opExtrude","SWEPT_BODY",BODY,{"disambiguationData":[OSD([sQuery(id+"F18.wireOp",EDGE,"E62.MirrorCS"),sQuery(id+"F18.wireOp",EDGE,"E63.MirrorCS"),sQuery(id+"F18.wireOp",EDGE,"E64.MirrorCS"),sQuery(id+"F18.wireOp",EDGE,"E65.MirrorCS"),sQuery(id+"F18.wireOp",EDGE,"E66.MirrorCS"),sQuery(id+"F18.wireOp",EDGE,"E67.MirrorCS")])]});
            var Q13;
            Q13=makeQuery(id+"F30.opExtrude","SWEPT_BODY",BODY,{"disambiguationData":[OSD([sQuery(id+"F29.wireOp",EDGE,"E89.bottom"),sQuery(id+"F29.wireOp",EDGE,"E89.top"),sQuery(id+"F29.wireOp",EDGE,"E89.left"),sQuery(id+"F29.wireOp",EDGE,"E89.right")])]});
            var Q14;
            Q14=makeQuery(id+"F47.opExtrude","SWEPT_BODY",BODY,{"disambiguationData":[OSD([sQuery(id+"F46.wireOp",EDGE,"E132"),sQuery(id+"F46.wireOp",EDGE,"E133"),sQuery(id+"F46.wireOp",EDGE,"E134"),sQuery(id+"F46.wireOp",EDGE,"E135"),sQuery(id+"F46.wireOp",EDGE,"E136"),sQuery(id+"F46.wireOp",EDGE,"E138")])]});
            var Q15;
            Q15=makeQuery(id+"F19.opExtrude","SWEPT_BODY",BODY,{"disambiguationData":[OSD([sQuery(id+"F18.wireOp",EDGE,"E68.MirrorCS"),sQuery(id+"F18.wireOp",EDGE,"E69.MirrorCS"),sQuery(id+"F18.wireOp",EDGE,"E70.MirrorCS"),sQuery(id+"F18.wireOp",EDGE,"E71.MirrorCS"),sQuery(id+"F18.wireOp",EDGE,"E72.MirrorCS"),sQuery(id+"F18.wireOp",EDGE,"E73.MirrorCS")])]});
            var Q16;
            Q16=qCreatedBy(id+"F50.planeOp",FACE);
            mirror(context, id + "F51", {"entities" : qUnion([Q0, Q1, Q2, Q3, Q4, Q5, Q6, Q7, Q8, Q9, Q10, Q11, Q12, Q13, Q14, Q15]), "mirrorPlane" : qUnion([Q16])});
        }
    });
